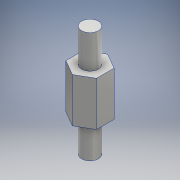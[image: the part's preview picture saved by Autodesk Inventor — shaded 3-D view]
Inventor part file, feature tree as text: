
AUTODESK INVENTOR PART (.ipt)
format: ipt  version: 2016 (Build 200138000, 138)  size: 107,520 bytes
history: native  units: mm
features: extrude x3, sketch x2, other x1
ambient origin geometry x8: Origin, YZ Plane, XZ Plane, XY Plane, X Axis, Y Axis, Z Axis, Center Point
bodies: Body1 (feature_tree)
feature tree (6):
  other  "ソリッド1"
  sketch  "スケッチ1"
  extrude  "押し出し1"  Depth=5.5mm
  extrude  "押し出し2"  Depth=3.0mm
  extrude  "押し出し3"  Depth=8.0mm TaperAngle=0.0deg
  sketch  "スケッチ2"
